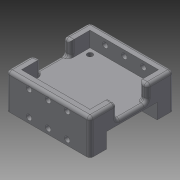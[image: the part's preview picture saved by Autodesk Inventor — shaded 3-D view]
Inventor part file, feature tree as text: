
AUTODESK INVENTOR PART (.ipt)
format: ipt  version: 2015 (Build 190159000, 159)  size: 254,976 bytes
history: native  units: in
note: dims shown in document units (in); Inventor stores cm internally (conversion verified against a paired STEP export)
features: extrude x6, sketch x6, fillet x1
ambient origin geometry x8: Origin, YZ Plane, XZ Plane, XY Plane, X Axis, Y Axis, Z Axis, Center Point
bodies: Solid1 (feature_tree)
feature tree (13):
  extrude  "Extrusion1"  Depth=0.15in TaperAngle=0.0deg
  extrude  "Extrusion2"  Depth=2.2441in
  extrude  "Extrusion3"  Depth=0.25in
  extrude  "Extrusion4"  Depth=0.1772in
  extrude  "Extrusion5"  Depth=1.25in
  extrude  "Extrusion6"  Depth=0.1in TaperAngle=0.0deg
  fillet  "Fillet1"  Radius=0.1772in
  sketch  "Sketch1"  dims[d0=0.5in d1=0.0in d2=0.15in d3=0.0in]
  sketch  "Sketch2"  dims[d4=0.5in d5=0.0in d6=2.2441in]
  sketch  "Sketch3"  dims[d7=2.2441in d8=0.25in]
  sketch  "Sketch4"  dims[d10=1.6535in d38=0.1772in]
  sketch  "Sketch5"  dims[d39=0.1772in d41=1.25in]
  sketch  "Sketch6"  dims[d42=0.4in d43=1.0in d44=0.0in d45=0.1772in d46=1.8559in d47=1.8559in d48=0.5in d49=0.0in d51=0.5in d52=0.0in d53=1.0in d54=0.1in]
